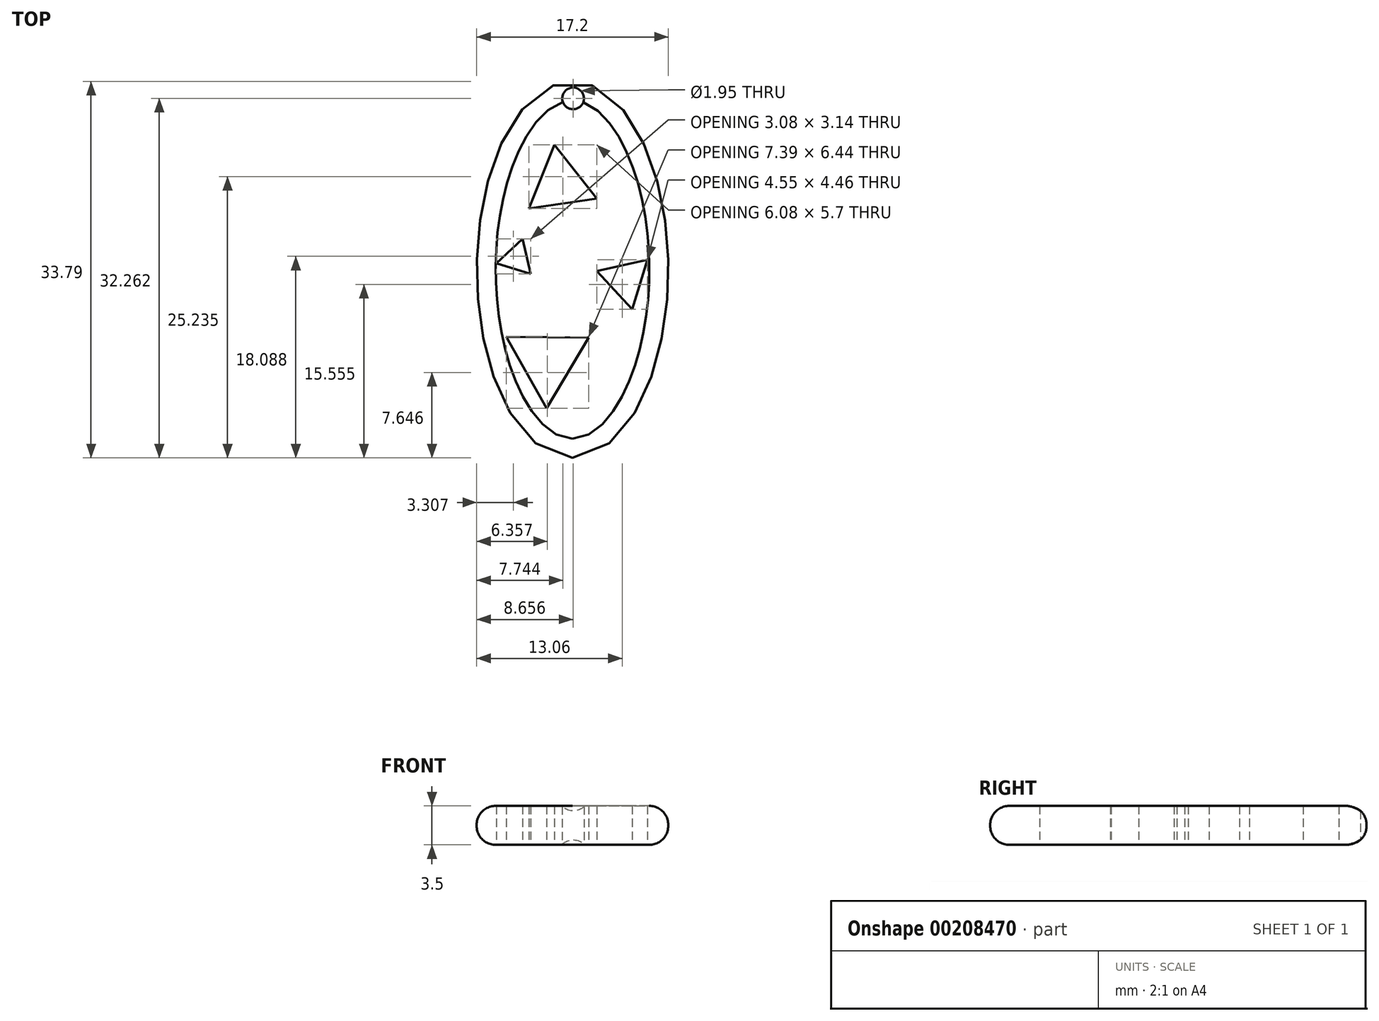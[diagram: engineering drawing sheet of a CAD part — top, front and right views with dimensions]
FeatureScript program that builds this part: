
annotation { "Feature Type Name" : "Feature", "Feature Type Description" : "" }
export const myFeature = defineFeature(function(context is Context, id is Id, definition is map)
    precondition{}
    {
        {
            var Q0;
            Q0=qCreatedBy(makeId("Top.planeOp"),FACE);
            var sketch = newSketch(context, id + "F0", { "sketchPlane" : qUnion([Q0])});
            skEllipse(sketch, "E0", {"center": v(-49.56, 46.27) * mm, "majorRadius": 16.9 * mm, "minorRadius": 8.6 * mm, "majorAxis": v(0, -1)});
            skCircle(sketch, "E1.cCircle", {"center": v(-50.67, 53.95) * mm, "radius": 3.55 * mm, "construction": true});
            skLineSegment(sketch, "E1.0", {"start": v(-51.17, 57.47) * mm, "end": v(-47.38, 52.63) * mm});
            skLineSegment(sketch, "E1.1", {"start": v(-47.38, 52.63) * mm, "end": v(-53.46, 51.76) * mm});
            skLineSegment(sketch, "E1.2", {"start": v(-53.46, 51.76) * mm, "end": v(-51.17, 57.47) * mm});
            skCircle(sketch, "E2.cCircle", {"center": v(-44.8, 45.33) * mm, "radius": 2.7 * mm, "construction": true});
            skLineSegment(sketch, "E2.0", {"start": v(-47.38, 46.13) * mm, "end": v(-42.83, 47.16) * mm});
            skLineSegment(sketch, "E2.1", {"start": v(-42.83, 47.16) * mm, "end": v(-44.2, 42.7) * mm});
            skLineSegment(sketch, "E2.2", {"start": v(-44.2, 42.7) * mm, "end": v(-47.38, 46.13) * mm});
            skCircle(sketch, "E3.cCircle", {"center": v(-51.82, 38.07) * mm, "radius": 4.27 * mm, "construction": true});
            skLineSegment(sketch, "E3.0", {"start": v(-48.1, 40.17) * mm, "end": v(-51.87, 33.8) * mm});
            skLineSegment(sketch, "E3.1", {"start": v(-51.87, 33.8) * mm, "end": v(-55.5, 40.24) * mm});
            skLineSegment(sketch, "E3.2", {"start": v(-55.5, 40.24) * mm, "end": v(-48.1, 40.17) * mm});
            skCircle(sketch, "E4", {"center": v(-49.5, 61.64) * mm, "radius": 0.98 * mm});
            skCircle(sketch, "E5.cCircle", {"center": v(-54.58, 47.26) * mm, "radius": 1.86 * mm, "construction": true});
            skLineSegment(sketch, "E5.0", {"start": v(-53.31, 45.9) * mm, "end": v(-56.4, 46.84) * mm});
            skLineSegment(sketch, "E5.1", {"start": v(-56.4, 46.84) * mm, "end": v(-54.04, 49.04) * mm});
            skLineSegment(sketch, "E5.2", {"start": v(-54.04, 49.04) * mm, "end": v(-53.31, 45.9) * mm});
            skSolve(sketch);
        }
        {
            var Q0;
            Q0 = qSketchRegion(id + "F0", true);
            var Q1;
            Q1=makeQuery(id+"F0.imprint","IMPRINT",FACE,{"disambiguationData":[TD([[makeQuery(id+"F0.imprint","IMPRINT",EDGE,{"derivedFrom":sQuery(id+"F0.wireOp",EDGE,"E0")}),1.0]])]});
            extrude(context, id + "F1", {"entities" : qUnion([Q0, Q1]), "depth" : 3.5 * mm});
        }
        {
            var Q0;
            Q0=makeQuery(id+"F1.opExtrude","CAP_EDGE",EDGE,{"disambiguationData":[OSD([sQuery(id+"F0.wireOp",EDGE,"E0")])],"isStart":true});
            fillet(context, id + "F2", {"entities" : qUnion([Q0]), "radius" : 1.7 * mm, "tangentPropagation" : true, "allowEdgeOverflow" : false});
        }
        {
            var Q0;
            Q0=makeQuery(id+"F1.opExtrude","CAP_EDGE",EDGE,{"disambiguationData":[OSD([sQuery(id+"F0.wireOp",EDGE,"E0")])],"isStart":false});
            fillet(context, id + "F3", {"entities" : qUnion([Q0]), "radius" : 1.7 * mm, "tangentPropagation" : true, "allowEdgeOverflow" : false});
        }
    });
